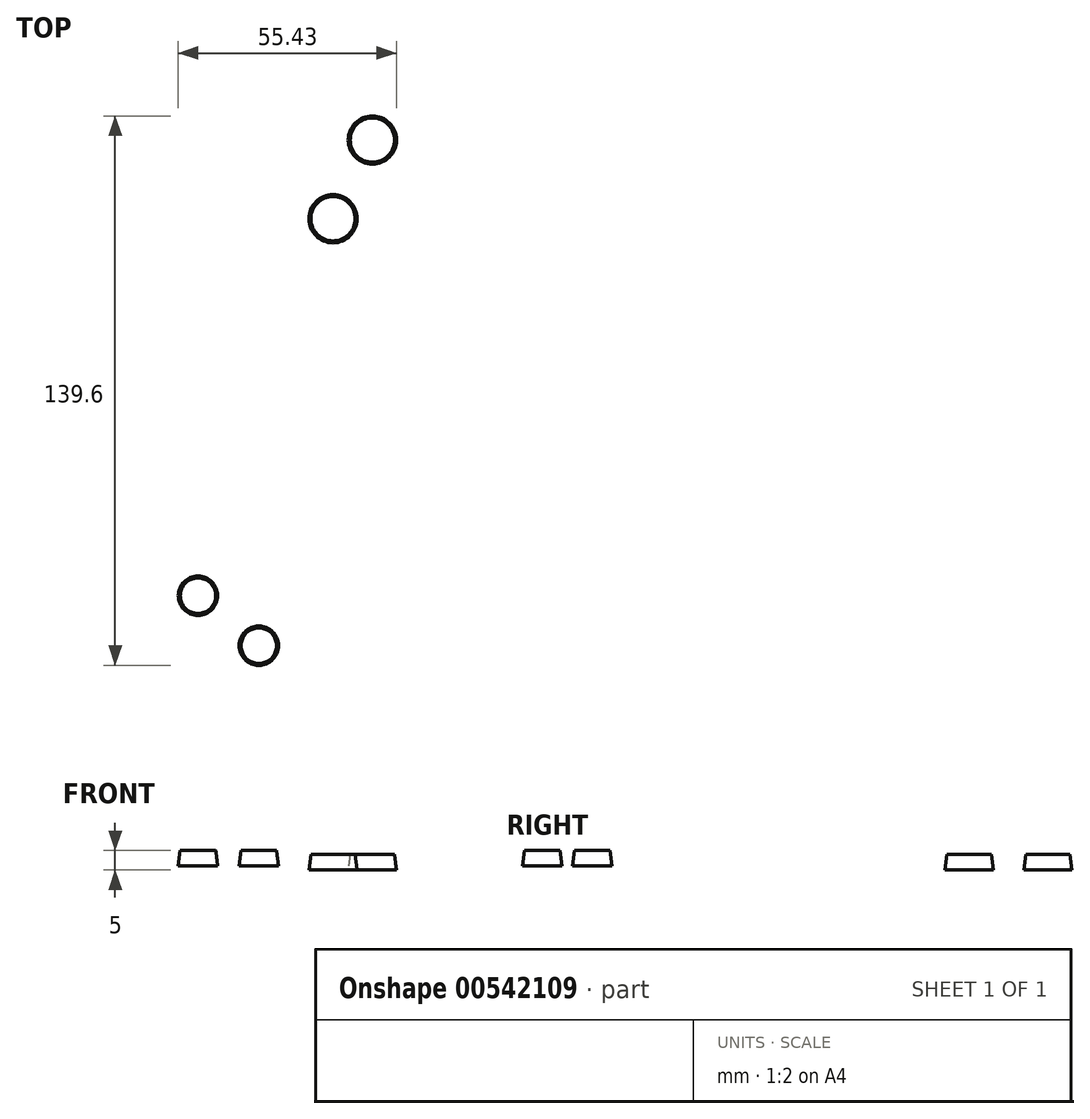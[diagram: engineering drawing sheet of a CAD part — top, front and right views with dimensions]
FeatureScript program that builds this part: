
annotation { "Feature Type Name" : "Feature", "Feature Type Description" : "" }
export const myFeature = defineFeature(function(context is Context, id is Id, definition is map)
    precondition{}
    {
        {
            var Q0;
            Q0=qCreatedBy(makeId("Front.planeOp"),FACE);
            var sketch = newSketch(context, id + "F0", { "sketchPlane" : qUnion([Q0])});
            skLineSegment(sketch, "E0", {"start": v(0, -1) * mm, "end": v(6.12, -1) * mm});
            skLineSegment(sketch, "E1", {"start": v(6.12, -1) * mm, "end": v(5.62, 3) * mm});
            skLineSegment(sketch, "E2", {"start": v(5.62, 3) * mm, "end": v(0, 3) * mm});
            skLineSegment(sketch, "E3", {"start": v(0, 3) * mm, "end": v(0, -1) * mm});
            skSolve(sketch);
        }
        {
            var Q0;
            Q0=makeQuery(id+"F0.imprint","IMPRINT",FACE,{"disambiguationData":[TD([[makeQuery(id+"F0.imprint","IMPRINT",EDGE,{"derivedFrom":sQuery(id+"F0.wireOp",EDGE,"E0")}),1.0]])]});
            var Q1;
            Q1=sQuery(id+"F0.wireOp",EDGE,"E3");
            revolve(context, id + "F1", {"entities" : qUnion([Q0]), "axis" : qUnion([Q1]), "revolveType" : RevolveType.FULL});
        }
        {
            var Q0;
            Q0=qCreatedBy(makeId("Top.planeOp"),FACE);
            var sketch = newSketch(context, id + "F2", { "sketchPlane" : qUnion([Q0])});
            skPoint(sketch, "E4", {"position": v(0, 15) * mm});
            skPoint(sketch, "E5", {"position": v(13, 7.5) * mm});
            skSolve(sketch);
        }
        {
            var Q0;
            Q0=qCreatedBy(makeId("Top.planeOp"),FACE);
            var sketch = newSketch(context, id + "F3", { "sketchPlane" : qUnion([Q0])});
            skCircle(sketch, "E6", {"center": v(-34.3, -95.78) * mm, "radius": 5 * mm});
            skCircle(sketch, "E7", {"center": v(-18.84, -108.47) * mm, "radius": 5 * mm});
            skSolve(sketch);
        }
        {
            var Q0;
            Q0=makeQuery(id+"F3.imprint","IMPRINT",FACE,{"disambiguationData":[TD([[makeQuery(id+"F3.imprint","IMPRINT",EDGE,{"derivedFrom":sQuery(id+"F3.wireOp",EDGE,"E6")}),1.0]])]});
            var Q1;
            Q1=makeQuery(id+"F3.imprint","IMPRINT",FACE,{"disambiguationData":[TD([[makeQuery(id+"F3.imprint","IMPRINT",EDGE,{"derivedFrom":sQuery(id+"F3.wireOp",EDGE,"E7")}),1.0]])]});
            extrude(context, id + "F4", {"entities" : qUnion([Q0, Q1]), "depth" : 4 * mm, "offsetDistance" : 25 * mm, "hasDraft" : true, "draftAngle" : 7 * degree, "draftPullDirection" : true});
        }
        {
            var Q0;
            Q0=makeQuery(id+"F1.opRevolve","SWEPT_BODY",BODY,{"disambiguationData":[OSD([sQuery(id+"F0.wireOp",EDGE,"E0"),sQuery(id+"F0.wireOp",EDGE,"E1"),sQuery(id+"F0.wireOp",EDGE,"E2"),sQuery(id+"F0.wireOp",EDGE,"E3")])]});
            var Q1;
            Q1=sQuery(id+"F2.wireOp",VERTEX,"E5");
            var Q2;
            Q2=qCreatedBy(makeId("Right.planeOp"),FACE);
            transform(context, id + "F5", {"entities" : qUnion([Q0]), "transformType" : TransformType.TRANSLATION_3D, "dx" : 10 * mm, "dy" : 20 * mm, "dz" : 0 * mm, "makeCopy" : true});
        }
    });
